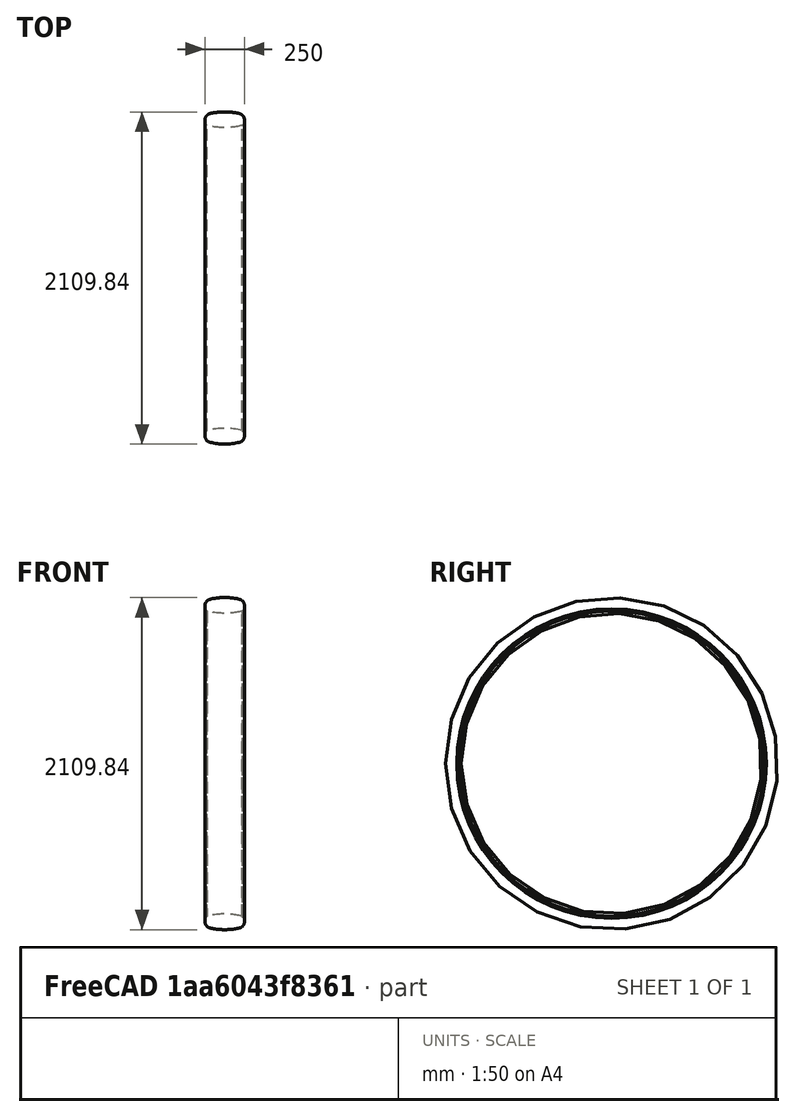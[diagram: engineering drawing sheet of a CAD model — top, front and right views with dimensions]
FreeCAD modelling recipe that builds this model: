
FCSTD DOCUMENT
Label: PR_011
objects: Sketcher::SketchObject×1, PartDesign::Revolution×1
note: 3 computed .brp shape members not serialized (recipe doc carries the construction recipe); baked Part::Feature solids carry a one-line shape summary decoded from their .brp

FEATURE [Sketcher::SketchObject] Sketch
  sketch-geometry (10):
    g0: LineSegment [constr] StartX=-194.452 StartY=-954.92 StartZ=0 EndX=551.146 EndY=-954.92 EndZ=0
    g1: LineSegment StartX=0 StartY=-982.931 StartZ=0 EndX=0 EndY=-1004.26 EndZ=0
    g2: LineSegment StartX=250 StartY=-982.931 StartZ=0 EndX=250 EndY=-1004.26 EndZ=0
    g3: LineSegment [constr] StartX=-263.211 StartY=-1054.92 StartZ=0 EndX=396.606 EndY=-1054.92 EndZ=0
    g4: ArcOfCircle CenterX=209 CenterY=-1004.26 CenterZ=0 NormalX=0 NormalY=0 NormalZ=1 Radius=41 StartAngle=4.94141 EndAngle=6.28319
    g5: ArcOfCircle CenterX=41 CenterY=-1004.26 CenterZ=0 NormalX=0 NormalY=0 NormalZ=1 Radius=41 StartAngle=3.14159 EndAngle=4.48337
    g6: ArcOfCircle CenterX=125 CenterY=-643.92 CenterZ=0 NormalX=0 NormalY=0 NormalZ=1 Radius=411 StartAngle=4.48337 EndAngle=4.94141
    g7: ArcOfCircle CenterX=125 CenterY=-1404.92 CenterZ=0 NormalX=0 NormalY=0 NormalZ=1 Radius=450 StartAngle=1.32188 EndAngle=1.81971
    g8: LineSegment StartX=235.858 StartY=-968.789 StartZ=0 EndX=250 EndY=-982.931 EndZ=0
    g9: LineSegment StartX=14.1421 StartY=-968.789 StartZ=0 EndX=0 EndY=-982.931 EndZ=0
  constraints (32):
    c: Horizontal(g0)
    c: DistanceY(g0) = -954.92
    c: Vertical(g1)
    c: Vertical(g2)
    c: DistanceX(g1) = 0
    c: DistanceX(g1,g2) = 250
    c: Horizontal(g3)
    c: DistanceY(g0,g3) = -100
    c: Radius(g4) = 41
    c: Radius(g5) = 41
    c: Tangent(g4,g2)
    c: Tangent(g1,g5)
    c: Tangent(g5,g6)
    c: Tangent(g6,g4)
    c: Tangent(g3,g6)
    c: Radius(g6) = 411
    c: Radius(g7) = 450
    c: Tangent(g0,g7)
    c: DistanceX(g6) = 125
    c: DistanceX(g7) = 125
    c: DistanceX(g3) = -263.211
    c: DistanceX(g0) = -194.452
    c: DistanceX(g0) = 551.146
    c: DistanceX(g3) = 396.606
    c: Coincident(g8,g7)
    c: Coincident(g9,g7)
    c: Coincident(g9,g1)
    c: Distance(g8) = 20
    c: Distance(g9) = 20
    c: Angle(g1,g9) = 2.35619
    c: Coincident(g8,g2)
    c: Angle(g8,g2) = 2.35619
FEATURE [PartDesign::Revolution] Revolution
  Angle = 360
  Axis = (1,0,0)
  Base = (0,0,0)
  ReferenceAxis = -> Sketch [H_Axis]
  Sketch = -> Sketch
